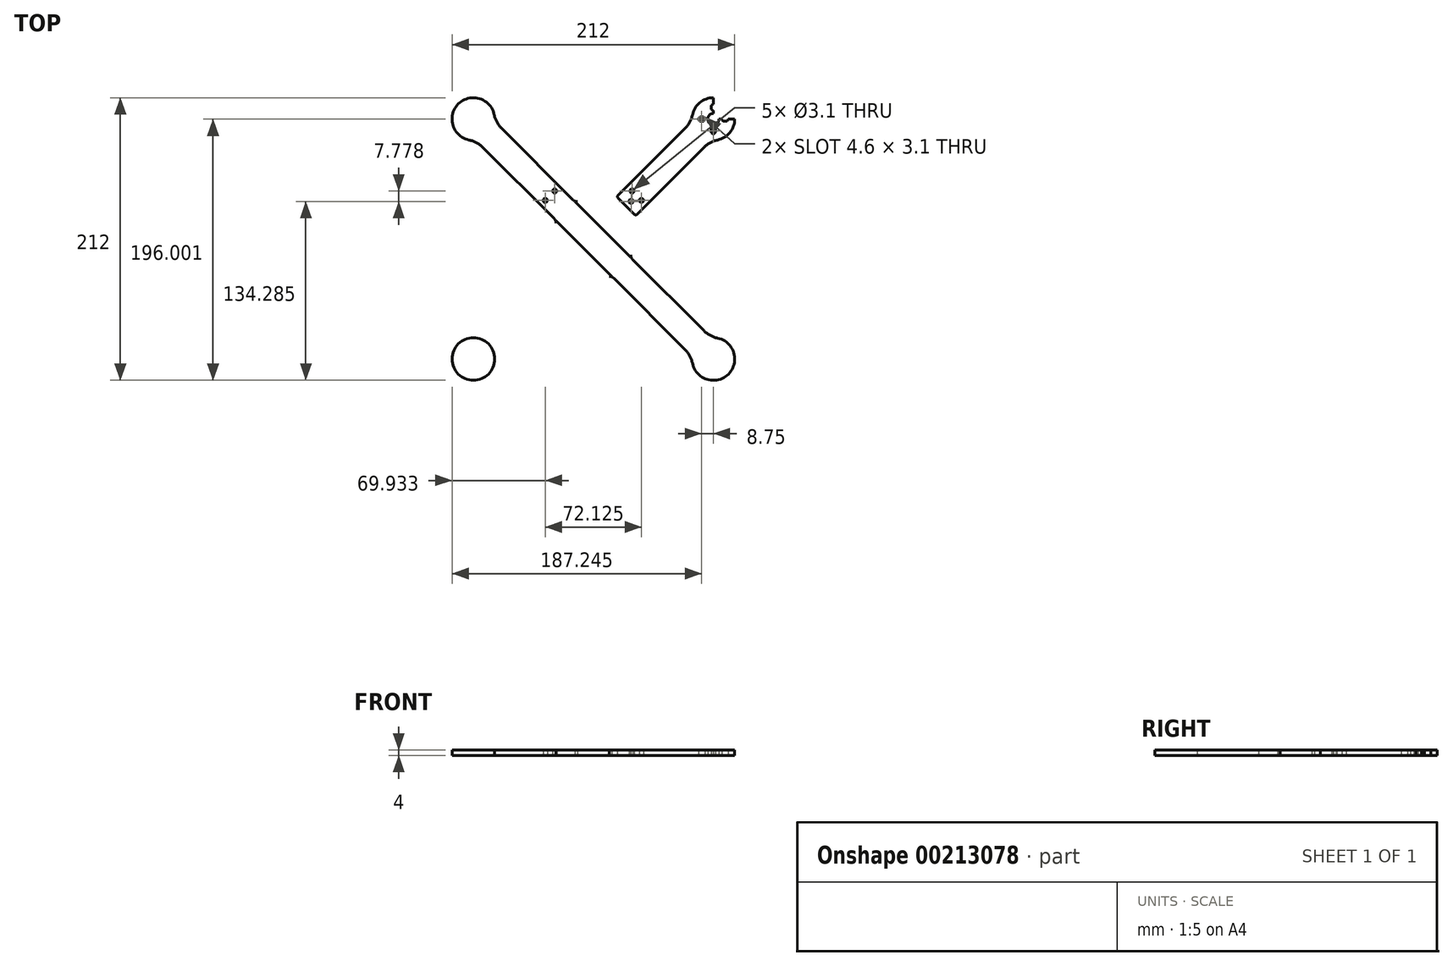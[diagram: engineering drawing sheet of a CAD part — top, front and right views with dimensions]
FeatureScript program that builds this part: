
annotation { "Feature Type Name" : "Feature", "Feature Type Description" : "" }
export const myFeature = defineFeature(function(context is Context, id is Id, definition is map)
    precondition{}
    {
        {
            var Q0;
            Q0=qCreatedBy(makeId("Top.planeOp"),FACE);
            var sketch = newSketch(context, id + "F0", { "sketchPlane" : qUnion([Q0])});
            skCircle(sketch, "E0", {"center": v(25.16, 68.17) * mm, "radius": 16 * mm});
            skCircle(sketch, "E1", {"center": v(-154.84, 68.17) * mm, "radius": 16 * mm});
            skCircle(sketch, "E2", {"center": v(-154.84, -111.83) * mm, "radius": 16 * mm});
            skCircle(sketch, "E3", {"center": v(25.16, -111.83) * mm, "radius": 16 * mm});
            skLineSegment(sketch, "E4", {"start": v(-154.84, 68.17) * mm, "end": v(25.16, -111.83) * mm});
            skLineSegment(sketch, "E5", {"start": v(-154.84, -111.83) * mm, "end": v(25.16, 68.17) * mm});
            skLineSegment(sketch, "E6", {"start": v(-138.94, 66.41) * mm, "end": v(23.4, -95.93) * mm});
            skLineSegment(sketch, "E7", {"start": v(-153.08, 52.27) * mm, "end": v(9.25, -110.07) * mm});
            skLineSegment(sketch, "E8", {"start": v(-46.46, 10.7) * mm, "end": v(9.25, 66.41) * mm});
            skLineSegment(sketch, "E9", {"start": v(-32.32, -3.44) * mm, "end": v(23.4, 52.27) * mm});
            skCircle(sketch, "E10", {"center": v(-161.99, 32.89) * mm, "radius": 20 * mm});
            skCircle(sketch, "E11", {"center": v(-119.56, 75.31) * mm, "radius": 20 * mm});
            skCircle(sketch, "E12", {"center": v(-10.13, 75.31) * mm, "radius": 20 * mm});
            skCircle(sketch, "E13", {"center": v(32.3, 32.89) * mm, "radius": 20 * mm});
            skCircle(sketch, "E14", {"center": v(32.3, -76.54) * mm, "radius": 20 * mm});
            skCircle(sketch, "E15", {"center": v(-10.13, -118.97) * mm, "radius": 20 * mm});
            skCircle(sketch, "E16", {"center": v(-119.56, -118.97) * mm, "radius": 20 * mm});
            skCircle(sketch, "E17", {"center": v(-161.99, -76.54) * mm, "radius": 20 * mm});
            skLineSegment(sketch, "E18", {"start": v(-92.84, -7.97) * mm, "end": v(-92.84, -35.69) * mm});
            skLineSegment(sketch, "E19", {"start": v(-36.84, -7.97) * mm, "end": v(-36.84, -35.69) * mm});
            skPoint(sketch, "E20", {"position": v(-64.84, -21.83) * mm});
            skCircle(sketch, "E21", {"center": v(-97.84, -10.04) * mm, "radius": 5 * mm});
            skCircle(sketch, "E22", {"center": v(-97.84, -33.62) * mm, "radius": 5 * mm});
            skCircle(sketch, "E23", {"center": v(-31.84, -10.04) * mm, "radius": 5 * mm});
            skCircle(sketch, "E24", {"center": v(-31.84, -33.62) * mm, "radius": 5 * mm});
            skLineSegment(sketch, "E25", {"start": v(-78.7, 6.17) * mm, "end": v(-50.99, 6.17) * mm});
            skLineSegment(sketch, "E26", {"start": v(-78.7, -49.83) * mm, "end": v(-50.99, -49.83) * mm});
            skCircle(sketch, "E27", {"center": v(-76.63, 11.17) * mm, "radius": 5 * mm});
            skCircle(sketch, "E28", {"center": v(-53.06, 11.17) * mm, "radius": 5 * mm});
            skCircle(sketch, "E29", {"center": v(-76.63, -54.83) * mm, "radius": 5 * mm});
            skCircle(sketch, "E30", {"center": v(-53.06, -54.83) * mm, "radius": 5 * mm});
            skLineSegment(sketch, "E31", {"start": v(-96.66, -4.15) * mm, "end": v(-82.52, 10) * mm});
            skCircle(sketch, "E32", {"center": v(-93.13, 6.46) * mm, "radius": 1.55 * mm});
            skCircle(sketch, "E33", {"center": v(-93.84, 14.23) * mm, "radius": 1.55 * mm});
            skCircle(sketch, "E34", {"center": v(-100.9, 7.16) * mm, "radius": 1.55 * mm});
            skLineSegment(sketch, "E35", {"start": v(-109.4, 8.58) * mm, "end": v(-95.25, 22.72) * mm});
            skLineSegment(sketch, "E36", {"start": v(-104.44, 3.63) * mm, "end": v(-90.3, 17.77) * mm});
            skLineSegment(sketch, "E37", {"start": v(-64.84, -7.69) * mm, "end": v(-64.84, -35.97) * mm});
            skLineSegment(sketch, "E38", {"start": v(-78.99, -21.83) * mm, "end": v(-50.7, -21.83) * mm});
            skLineSegment(sketch, "E39.MirrorCS", {"start": v(-33.73, -3.44) * mm, "end": v(-46.46, 9.28) * mm});
            skLineSegment(sketch, "E40.MirrorCS", {"start": v(-20.3, 8.58) * mm, "end": v(-34.44, 22.72) * mm});
            skLineSegment(sketch, "E41.MirrorCS", {"start": v(-25.25, 3.63) * mm, "end": v(-39.39, 17.77) * mm});
            skCircle(sketch, "E42.MirrorC", {"center": v(-35.85, 14.23) * mm, "radius": 1.55 * mm});
            skCircle(sketch, "E43.MirrorC", {"center": v(-36.56, 6.46) * mm, "radius": 1.55 * mm});
            skCircle(sketch, "E44.MirrorC", {"center": v(-28.78, 7.16) * mm, "radius": 1.55 * mm});
            skLineSegment(sketch, "E45", {"start": v(9.16, 68.17) * mm, "end": v(41.16, 68.17) * mm});
            skLineSegment(sketch, "E46", {"start": v(25.16, 84.17) * mm, "end": v(25.16, 52.17) * mm});
            skCircle(sketch, "E47", {"center": v(25.16, 68.17) * mm, "radius": 4.25 * mm});
            skCircle(sketch, "E48", {"center": v(25.16, 77.67) * mm, "radius": 1.55 * mm});
            skCircle(sketch, "E49", {"center": v(25.16, 76.17) * mm, "radius": 1.55 * mm});
            skCircle(sketch, "E50", {"center": v(33.16, 68.17) * mm, "radius": 1.55 * mm});
            skCircle(sketch, "E51", {"center": v(34.66, 68.17) * mm, "radius": 1.55 * mm});
            skLineSegment(sketch, "E52", {"start": v(23.6, 79.87) * mm, "end": v(23.6, 73.25) * mm});
            skLineSegment(sketch, "E53", {"start": v(26.7, 80.07) * mm, "end": v(26.7, 73.72) * mm});
            skLineSegment(sketch, "E54", {"start": v(31.07, 69.72) * mm, "end": v(36.67, 69.72) * mm});
            skLineSegment(sketch, "E55", {"start": v(30.6, 66.62) * mm, "end": v(37.89, 66.62) * mm});
            skCircle(sketch, "E56.MirrorC", {"center": v(25.16, 60.17) * mm, "radius": 1.55 * mm});
            skCircle(sketch, "E57.MirrorC", {"center": v(25.16, 58.67) * mm, "radius": 1.55 * mm});
            skLineSegment(sketch, "E58.MirrorCS", {"start": v(23.6, 56.47) * mm, "end": v(23.6, 63.1) * mm});
            skLineSegment(sketch, "E59.MirrorCS", {"start": v(26.7, 56.28) * mm, "end": v(26.7, 62.63) * mm});
            skCircle(sketch, "E60.MirrorC", {"center": v(17.16, 68.17) * mm, "radius": 1.55 * mm});
            skLineSegment(sketch, "E61.MirrorCS", {"start": v(19.24, 69.72) * mm, "end": v(13.64, 69.72) * mm});
            skCircle(sketch, "E62.MirrorC", {"center": v(15.66, 68.17) * mm, "radius": 1.55 * mm});
            skLineSegment(sketch, "E63.MirrorCS", {"start": v(19.7, 66.62) * mm, "end": v(12.42, 66.62) * mm});
            skPoint(sketch, "E64.newPointB", {"position": v(-47.17, 10) * mm});
            skArc(sketch, "E64.filletArc", {"start": v(-46.46, 10.7) * mm, "mid": v(-46.75, 10) * mm, "end": v(-46.46, 9.28) * mm});
            skPoint(sketch, "E65.newPointB", {"position": v(-33.02, -4.15) * mm});
            skArc(sketch, "E65.filletArc", {"start": v(-33.73, -3.44) * mm, "mid": v(-33.02, -3.74) * mm, "end": v(-32.32, -3.44) * mm});
            skSolve(sketch);
        }
        {
            var Q0;
            {var subQ0=sQuery(id+"F0.wireOp",EDGE,"E18");Q0=makeQuery(id+"F0.imprint","IMPRINT",FACE,{"disambiguationData":[TD([[makeQuery(id+"F0.imprint","IMPRINT",EDGE,{"derivedFrom":subQ0}),1.0]])]});}
            var Q1;
            {var subQ0=sQuery(id+"F0.wireOp",EDGE,"E8");var subQ1=sQuery(id+"F0.wireOp",EDGE,"E0");var subQ2=makeQuery(id+"F0.imprint","INTERSECT",VERTEX,{"derivedFrom":[subQ1,subQ0]});Q1=makeQuery(id+"F0.imprint","IMPRINT",FACE,{"disambiguationData":[TD([[makeQuery(id+"F0.imprint","IMPRINT",EDGE,{"disambiguationData":[TD([[subQ2,1.0]])],"derivedFrom":subQ1}),-1.0]])]});}
            var Q2;
            {var subQ0=sQuery(id+"F0.wireOp",EDGE,"E9");var subQ1=sQuery(id+"F0.wireOp",EDGE,"E0");var subQ2=makeQuery(id+"F0.imprint","INTERSECT",VERTEX,{"derivedFrom":[subQ1,subQ0]});Q2=makeQuery(id+"F0.imprint","IMPRINT",FACE,{"disambiguationData":[TD([[makeQuery(id+"F0.imprint","IMPRINT",EDGE,{"disambiguationData":[TD([[subQ2,-1.0]])],"derivedFrom":subQ1}),-1.0]])]});}
            var Q3;
            {var subQ0=sQuery(id+"F0.wireOp",EDGE,"E7");var subQ1=sQuery(id+"F0.wireOp",EDGE,"E1");var subQ2=makeQuery(id+"F0.imprint","INTERSECT",VERTEX,{"derivedFrom":[subQ1,subQ0]});Q3=makeQuery(id+"F0.imprint","IMPRINT",FACE,{"disambiguationData":[TD([[makeQuery(id+"F0.imprint","IMPRINT",EDGE,{"disambiguationData":[TD([[subQ2,1.0]])],"derivedFrom":subQ1}),-1.0]])]});}
            var Q4;
            {var subQ0=sQuery(id+"F0.wireOp",EDGE,"E6");var subQ1=sQuery(id+"F0.wireOp",EDGE,"E1");var subQ2=makeQuery(id+"F0.imprint","INTERSECT",VERTEX,{"derivedFrom":[subQ1,subQ0]});Q4=makeQuery(id+"F0.imprint","IMPRINT",FACE,{"disambiguationData":[TD([[makeQuery(id+"F0.imprint","IMPRINT",EDGE,{"disambiguationData":[TD([[subQ2,-1.0]])],"derivedFrom":subQ1}),-1.0]])]});}
            var Q5;
            {var subQ0=sQuery(id+"F0.wireOp",EDGE,"E8");var subQ1=sQuery(id+"F0.wireOp",EDGE,"E2");var subQ2=makeQuery(id+"F0.imprint","INTERSECT",VERTEX,{"derivedFrom":[subQ1,subQ0]});Q5=makeQuery(id+"F0.imprint","IMPRINT",FACE,{"disambiguationData":[TD([[makeQuery(id+"F0.imprint","IMPRINT",EDGE,{"disambiguationData":[TD([[subQ2,-1.0]])],"derivedFrom":subQ1}),-1.0]])]});}
            var Q6;
            {var subQ0=sQuery(id+"F0.wireOp",EDGE,"E9");var subQ1=sQuery(id+"F0.wireOp",EDGE,"E2");var subQ2=makeQuery(id+"F0.imprint","INTERSECT",VERTEX,{"derivedFrom":[subQ1,subQ0]});Q6=makeQuery(id+"F0.imprint","IMPRINT",FACE,{"disambiguationData":[TD([[makeQuery(id+"F0.imprint","IMPRINT",EDGE,{"disambiguationData":[TD([[subQ2,1.0]])],"derivedFrom":subQ1}),-1.0]])]});}
            var Q7;
            {var subQ0=sQuery(id+"F0.wireOp",EDGE,"E6");var subQ1=sQuery(id+"F0.wireOp",EDGE,"E3");var subQ2=makeQuery(id+"F0.imprint","INTERSECT",VERTEX,{"derivedFrom":[subQ1,subQ0]});Q7=makeQuery(id+"F0.imprint","IMPRINT",FACE,{"disambiguationData":[TD([[makeQuery(id+"F0.imprint","IMPRINT",EDGE,{"disambiguationData":[TD([[subQ2,1.0]])],"derivedFrom":subQ1}),-1.0]])]});}
            var Q8;
            {var subQ0=sQuery(id+"F0.wireOp",EDGE,"E7");var subQ1=sQuery(id+"F0.wireOp",EDGE,"E3");var subQ2=makeQuery(id+"F0.imprint","INTERSECT",VERTEX,{"derivedFrom":[subQ1,subQ0]});Q8=makeQuery(id+"F0.imprint","IMPRINT",FACE,{"disambiguationData":[TD([[makeQuery(id+"F0.imprint","IMPRINT",EDGE,{"disambiguationData":[TD([[subQ2,-1.0]])],"derivedFrom":subQ1}),-1.0]])]});}
            var Q9;
            {var subQ0=sQuery(id+"F0.wireOp",EDGE,"E0");var subQ4=makeQuery(id+"F0.imprint","INTERSECT",VERTEX,{"derivedFrom":[subQ0,sQuery(id+"F0.wireOp",EDGE,"E8")]});Q9=makeQuery(id+"F0.imprint","IMPRINT",FACE,{"disambiguationData":[TD([[makeQuery(id+"F0.imprint","IMPRINT",EDGE,{"disambiguationData":[TD([[subQ4,1.0]])],"derivedFrom":subQ0}),1.0]])]});}
            var Q10;
            {var subQ0=sQuery(id+"F0.wireOp",EDGE,"E8");var subQ6=sQuery(id+"F0.wireOp",EDGE,"E0");var subQ8=makeQuery(id+"F0.imprint","INTERSECT",VERTEX,{"derivedFrom":[subQ6,subQ0]});Q10=makeQuery(id+"F0.imprint","IMPRINT",FACE,{"disambiguationData":[TD([[makeQuery(id+"F0.imprint","IMPRINT",EDGE,{"disambiguationData":[TD([[subQ8,-1.0]])],"derivedFrom":subQ6}),-1.0]])]});}
            var Q11;
            {var subQ0=sQuery(id+"F0.wireOp",EDGE,"E1");var subQ4=makeQuery(id+"F0.imprint","INTERSECT",VERTEX,{"derivedFrom":[subQ0,sQuery(id+"F0.wireOp",EDGE,"E10")]});Q11=makeQuery(id+"F0.imprint","IMPRINT",FACE,{"disambiguationData":[TD([[makeQuery(id+"F0.imprint","IMPRINT",EDGE,{"disambiguationData":[TD([[subQ4,1.0]])],"derivedFrom":subQ0}),1.0]])]});}
            var Q12;
            {var subQ0=sQuery(id+"F0.wireOp",EDGE,"E6");var subQ4=sQuery(id+"F0.wireOp",EDGE,"E1");var subQ5=makeQuery(id+"F0.imprint","INTERSECT",VERTEX,{"derivedFrom":[subQ4,subQ0]});Q12=makeQuery(id+"F0.imprint","IMPRINT",FACE,{"disambiguationData":[TD([[makeQuery(id+"F0.imprint","IMPRINT",EDGE,{"disambiguationData":[TD([[subQ5,1.0]])],"derivedFrom":subQ4}),-1.0]])]});}
            var Q13;
            {var subQ0=sQuery(id+"F0.wireOp",EDGE,"E2");var subQ5=makeQuery(id+"F0.imprint","INTERSECT",VERTEX,{"derivedFrom":[subQ0,sQuery(id+"F0.wireOp",EDGE,"E9")]});Q13=makeQuery(id+"F0.imprint","IMPRINT",FACE,{"disambiguationData":[TD([[makeQuery(id+"F0.imprint","IMPRINT",EDGE,{"disambiguationData":[TD([[subQ5,-1.0]])],"derivedFrom":subQ0}),1.0]])]});}
            var Q14;
            {var subQ0=sQuery(id+"F0.wireOp",EDGE,"E9");var subQ1=sQuery(id+"F0.wireOp",EDGE,"E2");var subQ2=makeQuery(id+"F0.imprint","INTERSECT",VERTEX,{"derivedFrom":[subQ1,subQ0]});Q14=makeQuery(id+"F0.imprint","IMPRINT",FACE,{"disambiguationData":[TD([[makeQuery(id+"F0.imprint","IMPRINT",EDGE,{"disambiguationData":[TD([[subQ2,-1.0]])],"derivedFrom":subQ1}),-1.0]])]});}
            var Q15;
            {var subQ0=sQuery(id+"F0.wireOp",EDGE,"E3");var subQ4=makeQuery(id+"F0.imprint","INTERSECT",VERTEX,{"derivedFrom":[subQ0,sQuery(id+"F0.wireOp",EDGE,"E6")]});Q15=makeQuery(id+"F0.imprint","IMPRINT",FACE,{"disambiguationData":[TD([[makeQuery(id+"F0.imprint","IMPRINT",EDGE,{"disambiguationData":[TD([[subQ4,1.0]])],"derivedFrom":subQ0}),1.0]])]});}
            var Q16;
            {var subQ0=sQuery(id+"F0.wireOp",EDGE,"E7");var subQ1=sQuery(id+"F0.wireOp",EDGE,"E3");var subQ2=makeQuery(id+"F0.imprint","INTERSECT",VERTEX,{"derivedFrom":[subQ1,subQ0]});Q16=makeQuery(id+"F0.imprint","IMPRINT",FACE,{"disambiguationData":[TD([[makeQuery(id+"F0.imprint","IMPRINT",EDGE,{"disambiguationData":[TD([[subQ2,1.0]])],"derivedFrom":subQ1}),-1.0]])]});}
            var Q17;
            {var subQ0=sQuery(id+"F0.wireOp",EDGE,"E8");var subQ1=sQuery(id+"F0.wireOp",EDGE,"E4");var subQ2=makeQuery(id+"F0.imprint","INTERSECT",VERTEX,{"derivedFrom":[subQ1,subQ0]});Q17=makeQuery(id+"F0.imprint","IMPRINT",FACE,{"disambiguationData":[TD([[makeQuery(id+"F0.imprint","IMPRINT",EDGE,{"disambiguationData":[TD([[subQ2,-1.0]])],"derivedFrom":subQ1}),1.0]])]});}
            var Q18;
            {var subQ0=sQuery(id+"F0.wireOp",EDGE,"E5");var subQ1=sQuery(id+"F0.wireOp",EDGE,"E4");var subQ2=makeQuery(id+"F0.imprint","INTERSECT",VERTEX,{"derivedFrom":[subQ1,subQ0]});Q18=makeQuery(id+"F0.imprint","IMPRINT",FACE,{"disambiguationData":[TD([[makeQuery(id+"F0.imprint","IMPRINT",EDGE,{"disambiguationData":[TD([[subQ2,-1.0]])],"derivedFrom":subQ1}),-1.0]])]});}
            var Q19;
            {var subQ3=sQuery(id+"F0.wireOp",EDGE,"E9");var subQ5=sQuery(id+"F0.wireOp",EDGE,"E0");var subQ8=makeQuery(id+"F0.imprint","INTERSECT",VERTEX,{"derivedFrom":[subQ5,subQ3]});Q19=makeQuery(id+"F0.imprint","IMPRINT",FACE,{"disambiguationData":[TD([[makeQuery(id+"F0.imprint","IMPRINT",EDGE,{"disambiguationData":[TD([[subQ8,1.0]])],"derivedFrom":subQ5}),-1.0]])]});}
            var Q20;
            {var subQ0=sQuery(id+"F0.wireOp",EDGE,"E7");var subQ3=sQuery(id+"F0.wireOp",EDGE,"E1");var subQ4=makeQuery(id+"F0.imprint","INTERSECT",VERTEX,{"derivedFrom":[subQ3,subQ0]});Q20=makeQuery(id+"F0.imprint","IMPRINT",FACE,{"disambiguationData":[TD([[makeQuery(id+"F0.imprint","IMPRINT",EDGE,{"disambiguationData":[TD([[subQ4,-1.0]])],"derivedFrom":subQ3}),-1.0]])]});}
            var Q21;
            {var subQ0=sQuery(id+"F0.wireOp",EDGE,"E6");var subQ4=sQuery(id+"F0.wireOp",EDGE,"E3");var subQ9=makeQuery(id+"F0.imprint","INTERSECT",VERTEX,{"derivedFrom":[subQ4,subQ0]});Q21=makeQuery(id+"F0.imprint","IMPRINT",FACE,{"disambiguationData":[TD([[makeQuery(id+"F0.imprint","IMPRINT",EDGE,{"disambiguationData":[TD([[subQ9,-1.0]])],"derivedFrom":subQ4}),-1.0]])]});}
            var Q22;
            {var subQ0=sQuery(id+"F0.wireOp",EDGE,"E8");var subQ1=sQuery(id+"F0.wireOp",EDGE,"E4");var subQ2=makeQuery(id+"F0.imprint","INTERSECT",VERTEX,{"derivedFrom":[subQ1,subQ0]});Q22=makeQuery(id+"F0.imprint","IMPRINT",FACE,{"disambiguationData":[TD([[makeQuery(id+"F0.imprint","IMPRINT",EDGE,{"disambiguationData":[TD([[subQ2,-1.0]])],"derivedFrom":subQ1}),-1.0]])]});}
            var Q23;
            {var subQ0=sQuery(id+"F0.wireOp",EDGE,"E5");var subQ1=sQuery(id+"F0.wireOp",EDGE,"E4");var subQ2=makeQuery(id+"F0.imprint","INTERSECT",VERTEX,{"derivedFrom":[subQ1,subQ0]});Q23=makeQuery(id+"F0.imprint","IMPRINT",FACE,{"disambiguationData":[TD([[makeQuery(id+"F0.imprint","IMPRINT",EDGE,{"disambiguationData":[TD([[subQ2,-1.0]])],"derivedFrom":subQ1}),1.0]])]});}
            var Q24;
            {var subQ0=sQuery(id+"F0.wireOp",EDGE,"E18");var subQ1=sQuery(id+"F0.wireOp",EDGE,"E7");var subQ2=makeQuery(id+"F0.imprint","INTERSECT",VERTEX,{"derivedFrom":[subQ1,subQ0]});Q24=makeQuery(id+"F0.imprint","IMPRINT",FACE,{"disambiguationData":[TD([[makeQuery(id+"F0.imprint","IMPRINT",EDGE,{"disambiguationData":[TD([[subQ2,1.0]])],"derivedFrom":subQ1}),-1.0]])]});}
            var Q25;
            {var subQ0=sQuery(id+"F0.wireOp",EDGE,"E19");var subQ1=sQuery(id+"F0.wireOp",EDGE,"E9");var subQ2=makeQuery(id+"F0.imprint","INTERSECT",VERTEX,{"derivedFrom":[subQ1,subQ0]});Q25=makeQuery(id+"F0.imprint","IMPRINT",FACE,{"disambiguationData":[TD([[makeQuery(id+"F0.imprint","IMPRINT",EDGE,{"disambiguationData":[TD([[subQ2,-1.0]])],"derivedFrom":subQ1}),-1.0]])]});}
            var Q26;
            {var subQ0=sQuery(id+"F0.wireOp",EDGE,"E19");var subQ5=sQuery(id+"F0.wireOp",EDGE,"E6");var subQ7=makeQuery(id+"F0.imprint","INTERSECT",VERTEX,{"derivedFrom":[subQ5,subQ0]});Q26=makeQuery(id+"F0.imprint","IMPRINT",FACE,{"disambiguationData":[TD([[makeQuery(id+"F0.imprint","IMPRINT",EDGE,{"disambiguationData":[TD([[subQ7,1.0]])],"derivedFrom":subQ5}),1.0]])]});}
            var Q27;
            {var subQ0=sQuery(id+"F0.wireOp",EDGE,"E19");var subQ1=sQuery(id+"F0.wireOp",EDGE,"E6");var subQ2=makeQuery(id+"F0.imprint","INTERSECT",VERTEX,{"derivedFrom":[subQ1,subQ0]});Q27=makeQuery(id+"F0.imprint","IMPRINT",FACE,{"disambiguationData":[TD([[makeQuery(id+"F0.imprint","IMPRINT",EDGE,{"disambiguationData":[TD([[subQ2,-1.0]])],"derivedFrom":subQ1}),1.0]])]});}
            var Q28;
            {var subQ0=sQuery(id+"F0.wireOp",EDGE,"E18");var subQ1=sQuery(id+"F0.wireOp",EDGE,"E8");var subQ2=makeQuery(id+"F0.imprint","INTERSECT",VERTEX,{"derivedFrom":[subQ1,subQ0]});Q28=makeQuery(id+"F0.imprint","IMPRINT",FACE,{"disambiguationData":[TD([[makeQuery(id+"F0.imprint","IMPRINT",EDGE,{"disambiguationData":[TD([[subQ2,1.0]])],"derivedFrom":subQ1}),1.0]])]});}
            var Q29;
            {var subQ0=sQuery(id+"F0.wireOp",EDGE,"E8");var subQ1=sQuery(id+"F0.wireOp",EDGE,"E2");var subQ2=makeQuery(id+"F0.imprint","INTERSECT",VERTEX,{"derivedFrom":[subQ1,subQ0]});Q29=makeQuery(id+"F0.imprint","IMPRINT",FACE,{"disambiguationData":[TD([[makeQuery(id+"F0.imprint","IMPRINT",EDGE,{"disambiguationData":[TD([[subQ2,1.0]])],"derivedFrom":subQ1}),-1.0]])]});}
            var Q30;
            {var subQ0=sQuery(id+"F0.wireOp",EDGE,"E25");var subQ3=sQuery(id+"F0.wireOp",EDGE,"E6");var subQ4=makeQuery(id+"F0.imprint","INTERSECT",VERTEX,{"derivedFrom":[subQ3,subQ0]});Q30=makeQuery(id+"F0.imprint","IMPRINT",FACE,{"disambiguationData":[TD([[makeQuery(id+"F0.imprint","IMPRINT",EDGE,{"disambiguationData":[TD([[subQ4,-1.0]])],"derivedFrom":subQ3}),1.0]])]});}
            var Q31;
            {var subQ0=sQuery(id+"F0.wireOp",EDGE,"E25");var subQ1=sQuery(id+"F0.wireOp",EDGE,"E6");var subQ2=makeQuery(id+"F0.imprint","INTERSECT",VERTEX,{"derivedFrom":[subQ1,subQ0]});Q31=makeQuery(id+"F0.imprint","IMPRINT",FACE,{"disambiguationData":[TD([[makeQuery(id+"F0.imprint","IMPRINT",EDGE,{"disambiguationData":[TD([[subQ2,1.0]])],"derivedFrom":subQ1}),1.0]])]});}
            var Q32;
            {var subQ0=sQuery(id+"F0.wireOp",EDGE,"E25");var subQ1=sQuery(id+"F0.wireOp",EDGE,"E8");var subQ2=makeQuery(id+"F0.imprint","INTERSECT",VERTEX,{"derivedFrom":[subQ1,subQ0]});Q32=makeQuery(id+"F0.imprint","IMPRINT",FACE,{"disambiguationData":[TD([[makeQuery(id+"F0.imprint","IMPRINT",EDGE,{"disambiguationData":[TD([[subQ2,-1.0]])],"derivedFrom":subQ1}),1.0]])]});}
            var Q33;
            {var subQ0=sQuery(id+"F0.wireOp",EDGE,"E26");var subQ5=sQuery(id+"F0.wireOp",EDGE,"E7");var subQ7=makeQuery(id+"F0.imprint","INTERSECT",VERTEX,{"derivedFrom":[subQ5,subQ0]});Q33=makeQuery(id+"F0.imprint","IMPRINT",FACE,{"disambiguationData":[TD([[makeQuery(id+"F0.imprint","IMPRINT",EDGE,{"disambiguationData":[TD([[subQ7,1.0]])],"derivedFrom":subQ5}),-1.0]])]});}
            var Q34;
            {var subQ0=sQuery(id+"F0.wireOp",EDGE,"E26");var subQ1=sQuery(id+"F0.wireOp",EDGE,"E9");var subQ2=makeQuery(id+"F0.imprint","INTERSECT",VERTEX,{"derivedFrom":[subQ1,subQ0]});Q34=makeQuery(id+"F0.imprint","IMPRINT",FACE,{"disambiguationData":[TD([[makeQuery(id+"F0.imprint","IMPRINT",EDGE,{"disambiguationData":[TD([[subQ2,1.0]])],"derivedFrom":subQ1}),-1.0]])]});}
            var Q35;
            {var subQ0=sQuery(id+"F0.wireOp",EDGE,"E26");var subQ1=sQuery(id+"F0.wireOp",EDGE,"E7");var subQ2=makeQuery(id+"F0.imprint","INTERSECT",VERTEX,{"derivedFrom":[subQ1,subQ0]});Q35=makeQuery(id+"F0.imprint","IMPRINT",FACE,{"disambiguationData":[TD([[makeQuery(id+"F0.imprint","IMPRINT",EDGE,{"disambiguationData":[TD([[subQ2,-1.0]])],"derivedFrom":subQ1}),-1.0]])]});}
            var Q36;
            {var subQ3=sQuery(id+"F0.wireOp",EDGE,"E36");var subQ5=sQuery(id+"F0.wireOp",EDGE,"E4");var subQ6=makeQuery(id+"F0.imprint","INTERSECT",VERTEX,{"derivedFrom":[subQ5,subQ3]});Q36=makeQuery(id+"F0.imprint","IMPRINT",FACE,{"disambiguationData":[TD([[makeQuery(id+"F0.imprint","IMPRINT",EDGE,{"disambiguationData":[TD([[subQ6,-1.0]])],"derivedFrom":subQ5}),-1.0]])]});}
            var Q37;
            {var subQ0=sQuery(id+"F0.wireOp",EDGE,"E35");var subQ3=sQuery(id+"F0.wireOp",EDGE,"E4");var subQ4=makeQuery(id+"F0.imprint","INTERSECT",VERTEX,{"derivedFrom":[subQ3,subQ0]});Q37=makeQuery(id+"F0.imprint","IMPRINT",FACE,{"disambiguationData":[TD([[makeQuery(id+"F0.imprint","IMPRINT",EDGE,{"disambiguationData":[TD([[subQ4,-1.0]])],"derivedFrom":subQ3}),-1.0]])]});}
            var Q38;
            {var subQ4=sQuery(id+"F0.wireOp",EDGE,"E35");var subQ7=sQuery(id+"F0.wireOp",EDGE,"E4");var subQ8=makeQuery(id+"F0.imprint","INTERSECT",VERTEX,{"derivedFrom":[subQ7,subQ4]});Q38=makeQuery(id+"F0.imprint","IMPRINT",FACE,{"disambiguationData":[TD([[makeQuery(id+"F0.imprint","IMPRINT",EDGE,{"disambiguationData":[TD([[subQ8,-1.0]])],"derivedFrom":subQ7}),1.0]])]});}
            var Q39;
            {var subQ3=sQuery(id+"F0.wireOp",EDGE,"E36");var subQ5=sQuery(id+"F0.wireOp",EDGE,"E4");var subQ6=makeQuery(id+"F0.imprint","INTERSECT",VERTEX,{"derivedFrom":[subQ5,subQ3]});Q39=makeQuery(id+"F0.imprint","IMPRINT",FACE,{"disambiguationData":[TD([[makeQuery(id+"F0.imprint","IMPRINT",EDGE,{"disambiguationData":[TD([[subQ6,-1.0]])],"derivedFrom":subQ5}),1.0]])]});}
            var Q40;
            {var subQ4=sQuery(id+"F0.wireOp",EDGE,"E4");var subQ7=sQuery(id+"F0.wireOp",EDGE,"E31");var subQ9=makeQuery(id+"F0.imprint","INTERSECT",VERTEX,{"derivedFrom":[subQ4,subQ7]});Q40=makeQuery(id+"F0.imprint","IMPRINT",FACE,{"disambiguationData":[TD([[makeQuery(id+"F0.imprint","IMPRINT",EDGE,{"disambiguationData":[TD([[subQ9,-1.0]])],"derivedFrom":subQ4}),1.0]])]});}
            var Q41;
            {var subQ4=sQuery(id+"F0.wireOp",EDGE,"E31");var subQ7=sQuery(id+"F0.wireOp",EDGE,"E4");var subQ8=makeQuery(id+"F0.imprint","INTERSECT",VERTEX,{"derivedFrom":[subQ7,subQ4]});Q41=makeQuery(id+"F0.imprint","IMPRINT",FACE,{"disambiguationData":[TD([[makeQuery(id+"F0.imprint","IMPRINT",EDGE,{"disambiguationData":[TD([[subQ8,-1.0]])],"derivedFrom":subQ7}),-1.0]])]});}
            var Q42;
            {var subQ0=sQuery(id+"F0.wireOp",EDGE,"E7");var subQ1=sQuery(id+"F0.wireOp",EDGE,"E5");var subQ2=makeQuery(id+"F0.imprint","INTERSECT",VERTEX,{"derivedFrom":[subQ1,subQ0]});Q42=makeQuery(id+"F0.imprint","IMPRINT",FACE,{"disambiguationData":[TD([[makeQuery(id+"F0.imprint","IMPRINT",EDGE,{"disambiguationData":[TD([[subQ2,-1.0]])],"derivedFrom":subQ0}),1.0]])]});}
            var Q43;
            {var subQ0=sQuery(id+"F0.wireOp",EDGE,"E6");var subQ1=sQuery(id+"F0.wireOp",EDGE,"E5");var subQ2=makeQuery(id+"F0.imprint","INTERSECT",VERTEX,{"derivedFrom":[subQ1,subQ0]});Q43=makeQuery(id+"F0.imprint","IMPRINT",FACE,{"disambiguationData":[TD([[makeQuery(id+"F0.imprint","IMPRINT",EDGE,{"disambiguationData":[TD([[subQ2,1.0]])],"derivedFrom":subQ0}),-1.0]])]});}
            var Q44;
            {var subQ0=sQuery(id+"F0.wireOp",EDGE,"E6");var subQ1=sQuery(id+"F0.wireOp",EDGE,"E5");var subQ2=makeQuery(id+"F0.imprint","INTERSECT",VERTEX,{"derivedFrom":[subQ1,subQ0]});Q44=makeQuery(id+"F0.imprint","IMPRINT",FACE,{"disambiguationData":[TD([[makeQuery(id+"F0.imprint","IMPRINT",EDGE,{"disambiguationData":[TD([[subQ2,-1.0]])],"derivedFrom":subQ0}),-1.0]])]});}
            var Q45;
            {var subQ0=sQuery(id+"F0.wireOp",EDGE,"E39.MirrorCS");var subQ3=sQuery(id+"F0.wireOp",EDGE,"E5");var subQ4=makeQuery(id+"F0.imprint","INTERSECT",VERTEX,{"derivedFrom":[subQ3,subQ0]});Q45=makeQuery(id+"F0.imprint","IMPRINT",FACE,{"disambiguationData":[TD([[makeQuery(id+"F0.imprint","IMPRINT",EDGE,{"disambiguationData":[TD([[subQ4,-1.0]])],"derivedFrom":subQ3}),1.0]])]});}
            var Q46;
            {var subQ0=sQuery(id+"F0.wireOp",EDGE,"E41.MirrorCS");var subQ1=sQuery(id+"F0.wireOp",EDGE,"E5");var subQ2=makeQuery(id+"F0.imprint","INTERSECT",VERTEX,{"derivedFrom":[subQ1,subQ0]});Q46=makeQuery(id+"F0.imprint","IMPRINT",FACE,{"disambiguationData":[TD([[makeQuery(id+"F0.imprint","IMPRINT",EDGE,{"disambiguationData":[TD([[subQ2,-1.0]])],"derivedFrom":subQ1}),1.0]])]});}
            var Q47;
            {var subQ0=sQuery(id+"F0.wireOp",EDGE,"E41.MirrorCS");var subQ7=sQuery(id+"F0.wireOp",EDGE,"E5");var subQ9=makeQuery(id+"F0.imprint","INTERSECT",VERTEX,{"derivedFrom":[subQ7,subQ0]});Q47=makeQuery(id+"F0.imprint","IMPRINT",FACE,{"disambiguationData":[TD([[makeQuery(id+"F0.imprint","IMPRINT",EDGE,{"disambiguationData":[TD([[subQ9,-1.0]])],"derivedFrom":subQ7}),-1.0]])]});}
            var Q48;
            {var subQ0=sQuery(id+"F0.wireOp",EDGE,"E39.MirrorCS");var subQ3=sQuery(id+"F0.wireOp",EDGE,"E5");var subQ4=makeQuery(id+"F0.imprint","INTERSECT",VERTEX,{"derivedFrom":[subQ3,subQ0]});Q48=makeQuery(id+"F0.imprint","IMPRINT",FACE,{"disambiguationData":[TD([[makeQuery(id+"F0.imprint","IMPRINT",EDGE,{"disambiguationData":[TD([[subQ4,-1.0]])],"derivedFrom":subQ3}),-1.0]])]});}
            var Q49;
            {var subQ0=sQuery(id+"F0.wireOp",EDGE,"E7");var subQ1=sQuery(id+"F0.wireOp",EDGE,"E5");var subQ2=makeQuery(id+"F0.imprint","INTERSECT",VERTEX,{"derivedFrom":[subQ1,subQ0]});Q49=makeQuery(id+"F0.imprint","IMPRINT",FACE,{"disambiguationData":[TD([[makeQuery(id+"F0.imprint","IMPRINT",EDGE,{"disambiguationData":[TD([[subQ2,1.0]])],"derivedFrom":subQ0}),1.0]])]});}
            var Q50;
            {var subQ3=sQuery(id+"F0.wireOp",EDGE,"E45");var subQ19=sQuery(id+"F0.wireOp",EDGE,"E0");var subQ20=makeQuery(id+"F0.imprint","INTERSECT",VERTEX,{"disambiguationData":[OD(1.0)],"derivedFrom":[subQ19,subQ3]});Q50=makeQuery(id+"F0.imprint","IMPRINT",FACE,{"disambiguationData":[TD([[makeQuery(id+"F0.imprint","IMPRINT",EDGE,{"disambiguationData":[TD([[subQ20,-1.0]])],"derivedFrom":subQ19}),1.0]])]});}
            var Q51;
            {var subQ0=sQuery(id+"F0.wireOp",EDGE,"E46");var subQ1=sQuery(id+"F0.wireOp",EDGE,"E0");var subQ2=makeQuery(id+"F0.imprint","INTERSECT",VERTEX,{"disambiguationData":[OD(0.0)],"derivedFrom":[subQ1,subQ0]});Q51=makeQuery(id+"F0.imprint","IMPRINT",FACE,{"disambiguationData":[TD([[makeQuery(id+"F0.imprint","IMPRINT",EDGE,{"disambiguationData":[TD([[subQ2,-1.0]])],"derivedFrom":subQ1}),1.0]])]});}
            var Q52;
            {var subQ1=sQuery(id+"F0.wireOp",EDGE,"E0");var subQ6=sQuery(id+"F0.wireOp",EDGE,"E46");var subQ7=makeQuery(id+"F0.imprint","INTERSECT",VERTEX,{"disambiguationData":[OD(1.0)],"derivedFrom":[subQ1,subQ6]});Q52=makeQuery(id+"F0.imprint","IMPRINT",FACE,{"disambiguationData":[TD([[makeQuery(id+"F0.imprint","IMPRINT",EDGE,{"disambiguationData":[TD([[subQ7,-1.0]])],"derivedFrom":subQ1}),1.0]])]});}
            var Q53;
            {var subQ1=sQuery(id+"F0.wireOp",EDGE,"E0");var subQ8=makeQuery(id+"F0.imprint","INTERSECT",VERTEX,{"derivedFrom":[subQ1,sQuery(id+"F0.wireOp",EDGE,"E9")]});Q53=makeQuery(id+"F0.imprint","IMPRINT",FACE,{"disambiguationData":[TD([[makeQuery(id+"F0.imprint","IMPRINT",EDGE,{"disambiguationData":[TD([[subQ8,1.0]])],"derivedFrom":subQ1}),1.0]])]});}
            extrude(context, id + "F1", {"entities" : qUnion([Q0, Q1, Q2, Q3, Q4, Q5, Q6, Q7, Q8, Q9, Q10, Q11, Q12, Q13, Q14, Q15, Q16, Q17, Q18, Q19, Q20, Q21, Q22, Q23, Q24, Q25, Q26, Q27, Q28, Q29, Q30, Q31, Q32, Q33, Q34, Q35, Q36, Q37, Q38, Q39, Q40, Q41, Q42, Q43, Q44, Q45, Q46, Q47, Q48, Q49, Q50, Q51, Q52, Q53]), "depth" : 4 * mm});
        }
    });
